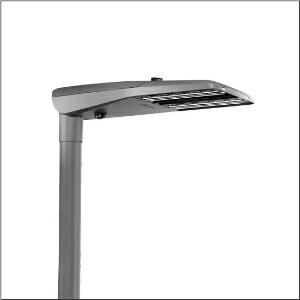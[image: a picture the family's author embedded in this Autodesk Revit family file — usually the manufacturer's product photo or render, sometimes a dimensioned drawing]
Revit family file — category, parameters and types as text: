
# Revit family: streetlight_sl_11_iq_midi___st1_0ab_5xc3n51y08le_be24
name_source: partatom
category: Lighting Fixtures
units: mm (PartAtom-declared; Revit-internal decimal feet)

## family parameters
Cut with Voids When Loaded = No
Host = Face
Light Source = No
Part Type = Normal
Room Calculation Point = No
Round Connector Dimension = Use Diameter
Shared = No

## types (1)
- --- (1 x LED, 7760 lm, 59.4 W, 3000K)
    Apparent Load = 59 VA
    CIE Flux Codes = 29 63 95 100 100
    Color Rendering = 70
    Color Temperature = 3000K
    Default Elevation = 1800 mm
    Description = Streetlight SL 11 iQ midi, mast luminaire, primary light control with 3 zone facetted reflector, of plastic, silver coated, highly specular, primary optical cover: cover, of PMMA, transparent, light distribution: ST1.0aB, light emission: direct distribution, primary light characteristic: asymmetric, installation type: post-top, side-entry, LED, High Power LED, rated luminous flux: 7.760lm, luminous efficacy: 131lm/W, light colour: 730, colour temperature: 3000K, control: pre-setting: logarithmic dimming characteristic, Street-Remote, Auto-Match, Temp-Guard, Lumen-Switch, Night-Set, Smart-Wire, Light-Fading, Desk-Remote (wireless, voltage-free reading and setting of iQ features in the workshop via application-optimized NFC function/RFID function), optimised constant luminous flux control (CLO 2.0), with cable H07RN-F 5x 1.5mm², mains connection: 230..240V, AC, 50/60Hz, connection cable pre-assembled, cable length: 8,5m, start of lifetime: 59W, end of service life: 62W, reduction: 29W, luminaire housing, of diecast aluminium, powder-coated, Siteco® metallic grey (DB 702S), please order mast flange separately, inclination adjustable without tools: 0°, 5°, 10°, 15° (post-top) | 0°, -5°, -10°, -15° (side-entry), sealing non-destructively replaceable, multi-level sealing system, length: 780mm, width: 376mm, height: 118mm, mast flange for spigot size: 42mm (side-entry): 5XC10008XM4, 60/48mm (side-entry/post-top): 5XC10108XM2, 76/60mm (side-entry/post-top): 5XC10108XM1, equipment: standard, Smart Interface below and above, protection rating (complete): IP66, insulation class (complete): insulation class II (safety insulation), certification: CE, ENEC, VDE, UKCA, impact resistance: IK09, permissible operating ambient temperature for outdoor applications: -25..+50°C, standard-compliant lighting for roads and squares, Environmental Product Declaration (EPD) tested and certified by an independent institute, packaging unit: 1 piece

Light Distribution: ST1.0aB
    Height = 118 mm
    Lamp = 1 x LED
    Lamp Light Flux = 7760 lm
    Lamp Power = 59.4 W
    Lamp count = 1
    Length = 780 mm
    Luminous efficacy = 131 lm/W
    Manufacturer = Siteco
    ModVariant = No
    Model = 5XC3N51Y08LE
    Number of Poles = 1
    OnlyDefault = Yes
    Power Factor = 1
    Product Name = Streetlight SL 11 iQ midi | ST1.0aB
    Product group = mast luminaire | pylon top
    ProductGroupID = 6100
    Protection Class = Protection class II
    Protection Degree = IP 66
    RLX_Detail_Level = 1
    RLX_Emergency_Light_Flux = 0 lm
    RLX_Emergency_Type = 0
    RLX_Emergency_Type_DB = No
    RlxData = <blob elided: 69205 chars, md5=f0a1e1e0>
    Socket = socket
    Standby Power = 0 W
    System Light Flux = 7760 lm
    System Power = 59 W
    Type Comments = factory setting: luminous flux: 100 % | dim-lin: 254 | 521 mA
    Type Image = l_1004429.jpg
    URL = http://relux.com
    VarID = @adj_056595
    Voltage = 0 V
    Weight = 0.00 kg
    Width = 376 mm

## geometry (parser evidence)
native form markers: Blend x4, Sweep x11
no freeform markers — native parametric forms only
